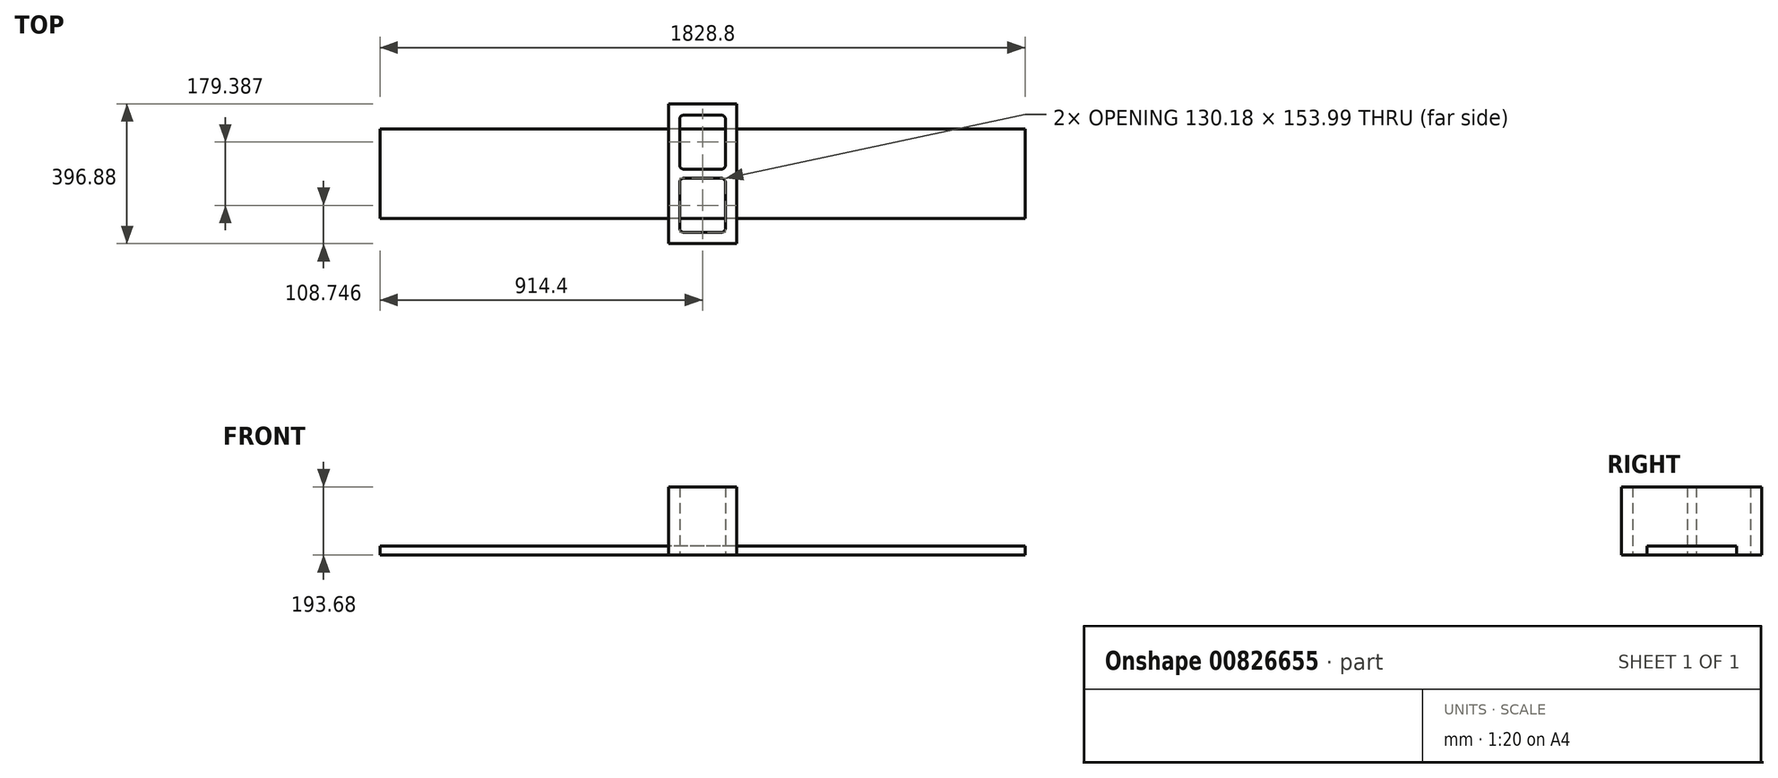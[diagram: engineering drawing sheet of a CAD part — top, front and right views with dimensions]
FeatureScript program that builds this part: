
annotation { "Feature Type Name" : "Feature", "Feature Type Description" : "" }
export const myFeature = defineFeature(function(context is Context, id is Id, definition is map)
    precondition{}
    {
        {
            var Q0;
            Q0=qCreatedBy(makeId("Top.planeOp"),FACE);
            var sketch = newSketch(context, id + "F0", { "sketchPlane" : qUnion([Q0])});
            skLineSegment(sketch, "E0.bottom", {"start": v(914.4, -127) * mm, "end": v(-914.4, -127) * mm});
            skLineSegment(sketch, "E0.top", {"start": v(914.4, 127) * mm, "end": v(-914.4, 127) * mm});
            skLineSegment(sketch, "E0.left", {"start": v(914.4, -127) * mm, "end": v(914.4, 127) * mm});
            skLineSegment(sketch, "E0.right", {"start": v(-914.4, -127) * mm, "end": v(-914.4, 127) * mm});
            skPoint(sketch, "E0.middle", {"position": v(0, 0) * mm});
            skSolve(sketch);
        }
        {
            var Q0;
            Q0=makeQuery(id+"F0.imprint","IMPRINT",FACE,{"disambiguationData":[TD([[makeQuery(id+"F0.imprint","IMPRINT",EDGE,{"derivedFrom":sQuery(id+"F0.wireOp",EDGE,"E0.bottom")}),-1.0]])]});
            extrude(context, id + "F1", {"entities" : qUnion([Q0]), "depth" : 25.4 * mm, "offsetDistance" : 25.4 * mm});
        }
        {
            var Q0;
            Q0=qCreatedBy(makeId("Top.planeOp"),FACE);
            var sketch = newSketch(context, id + "F2", { "sketchPlane" : qUnion([Q0])});
            skLineSegment(sketch, "E1.bottom", {"start": v(96.84, -198.44) * mm, "end": v(-96.84, -198.44) * mm});
            skLineSegment(sketch, "E1.top", {"start": v(96.84, 198.44) * mm, "end": v(-96.84, 198.44) * mm});
            skLineSegment(sketch, "E1.left", {"start": v(96.84, -198.44) * mm, "end": v(96.84, 198.44) * mm});
            skLineSegment(sketch, "E1.right", {"start": v(-96.84, -198.44) * mm, "end": v(-96.84, 198.44) * mm});
            skPoint(sketch, "E1.middle", {"position": v(0, 0) * mm});
            skLineSegment(sketch, "E2.bottom", {"start": v(52.39, 12.7) * mm, "end": v(-52.39, 12.7) * mm});
            skLineSegment(sketch, "E2.top", {"start": v(52.39, 166.69) * mm, "end": v(-52.39, 166.69) * mm});
            skLineSegment(sketch, "E2.left", {"start": v(65.09, 25.4) * mm, "end": v(65.09, 153.99) * mm});
            skLineSegment(sketch, "E2.right", {"start": v(-65.09, 25.4) * mm, "end": v(-65.09, 153.99) * mm});
            skPoint(sketch, "E2.middle", {"position": v(0, 89.7) * mm});
            skLineSegment(sketch, "E3.MirrorCS", {"start": v(52.39, -12.7) * mm, "end": v(-52.39, -12.7) * mm});
            skLineSegment(sketch, "E4.MirrorCS", {"start": v(65.09, -25.4) * mm, "end": v(65.09, -153.99) * mm});
            skLineSegment(sketch, "E5.MirrorCS", {"start": v(52.39, -166.69) * mm, "end": v(-52.39, -166.69) * mm});
            skLineSegment(sketch, "E6.MirrorCS", {"start": v(-65.09, -25.4) * mm, "end": v(-65.09, -153.99) * mm});
            skPoint(sketch, "E7.visualSharp", {"position": v(-65.09, 166.69) * mm});
            skArc(sketch, "E7.filletArc", {"start": v(-52.39, 166.69) * mm, "mid": v(-61.37, 162.97) * mm, "end": v(-65.09, 153.99) * mm});
            skPoint(sketch, "E8.visualSharp", {"position": v(65.09, 166.69) * mm});
            skArc(sketch, "E8.filletArc", {"start": v(65.09, 153.99) * mm, "mid": v(61.37, 162.97) * mm, "end": v(52.39, 166.69) * mm});
            skPoint(sketch, "E9.visualSharp", {"position": v(65.09, 12.7) * mm});
            skArc(sketch, "E9.filletArc", {"start": v(52.39, 12.7) * mm, "mid": v(61.37, 16.42) * mm, "end": v(65.09, 25.4) * mm});
            skPoint(sketch, "E10.visualSharp", {"position": v(-65.09, 12.7) * mm});
            skArc(sketch, "E10.filletArc", {"start": v(-65.09, 25.4) * mm, "mid": v(-61.37, 16.42) * mm, "end": v(-52.39, 12.7) * mm});
            skPoint(sketch, "E11.visualSharp", {"position": v(-65.09, -12.7) * mm});
            skArc(sketch, "E11.filletArc", {"start": v(-52.39, -12.7) * mm, "mid": v(-61.37, -16.42) * mm, "end": v(-65.09, -25.4) * mm});
            skPoint(sketch, "E12.visualSharp", {"position": v(-65.09, -166.69) * mm});
            skArc(sketch, "E12.filletArc", {"start": v(-65.09, -153.99) * mm, "mid": v(-61.37, -162.97) * mm, "end": v(-52.39, -166.69) * mm});
            skPoint(sketch, "E13.visualSharp", {"position": v(65.09, -12.7) * mm});
            skArc(sketch, "E13.filletArc", {"start": v(65.09, -25.4) * mm, "mid": v(61.37, -16.42) * mm, "end": v(52.39, -12.7) * mm});
            skPoint(sketch, "E14.visualSharp", {"position": v(65.09, -166.69) * mm});
            skArc(sketch, "E14.filletArc", {"start": v(52.39, -166.69) * mm, "mid": v(61.37, -162.97) * mm, "end": v(65.09, -153.99) * mm});
            skSolve(sketch);
        }
        {
            var Q0;
            Q0=makeQuery(id+"F2.imprint","IMPRINT",FACE,{"disambiguationData":[TD([[makeQuery(id+"F2.imprint","IMPRINT",EDGE,{"derivedFrom":sQuery(id+"F2.wireOp",EDGE,"E1.bottom")}),-1.0]])]});
            extrude(context, id + "F3", {"entities" : qUnion([Q0]), "depth" : 193.67 * mm, "offsetDistance" : 25.4 * mm});
        }
    });
